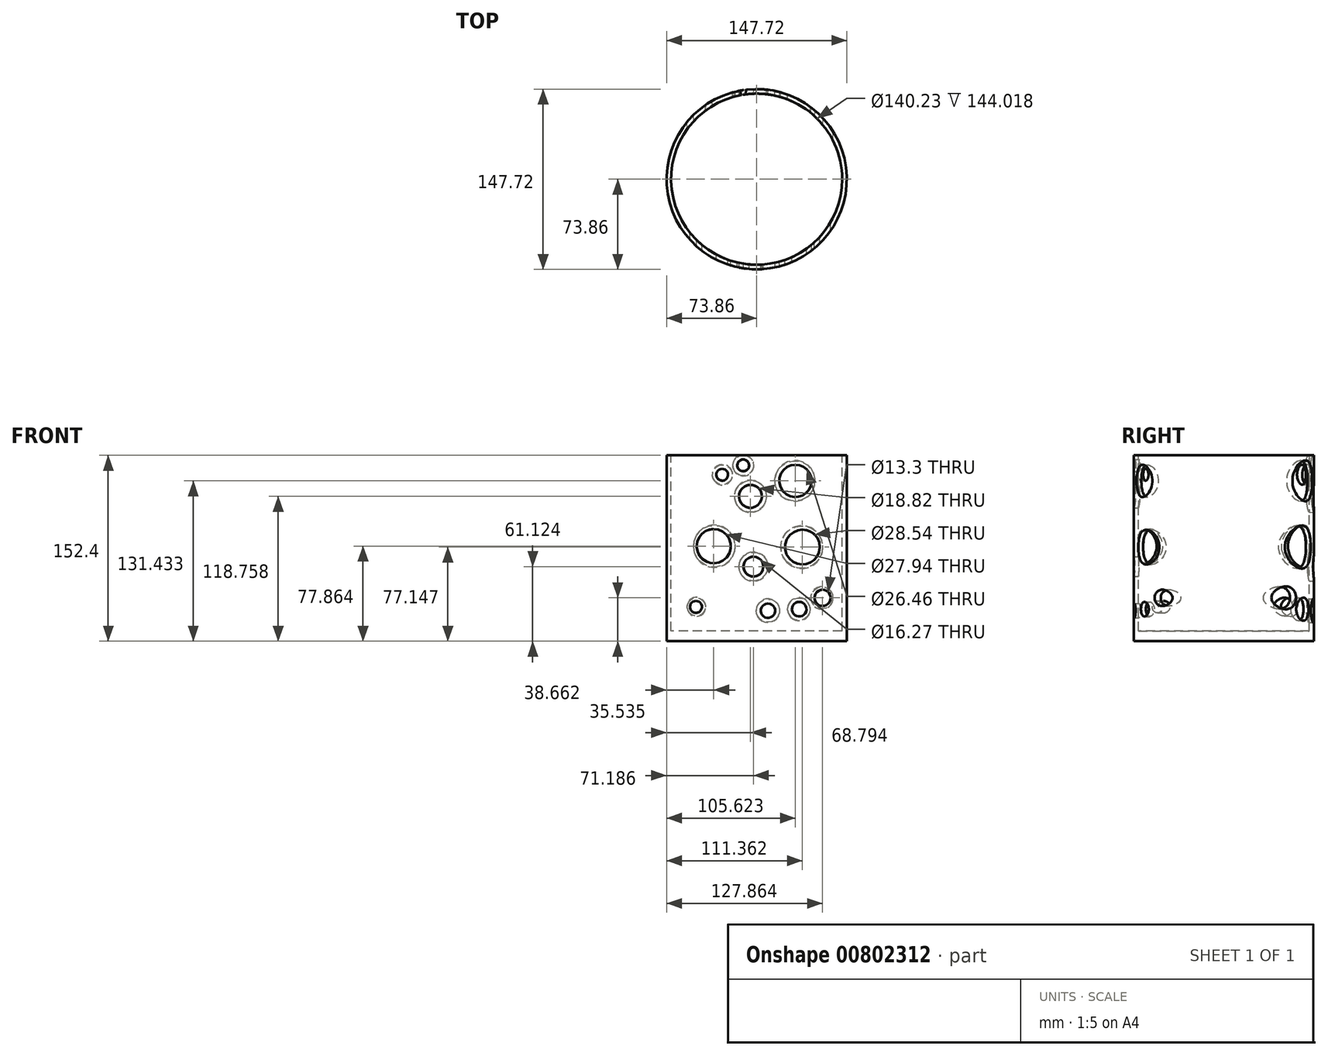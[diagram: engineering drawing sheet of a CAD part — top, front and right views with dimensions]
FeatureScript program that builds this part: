
annotation { "Feature Type Name" : "Feature", "Feature Type Description" : "" }
export const myFeature = defineFeature(function(context is Context, id is Id, definition is map)
    precondition{}
    {
        {
            var Q0;
            Q0=qCreatedBy(makeId("Top.planeOp"),FACE);
            var sketch = newSketch(context, id + "F0", { "sketchPlane" : qUnion([Q0])});
            skCircle(sketch, "E0", {"center": v(0, 0) * mm, "radius": 73.86 * mm});
            skSolve(sketch);
        }
        {
            var Q0;
            Q0=makeQuery(id+"F0.imprint","IMPRINT",FACE,{"disambiguationData":[TD([[makeQuery(id+"F0.imprint","IMPRINT",EDGE,{"derivedFrom":sQuery(id+"F0.wireOp",EDGE,"E0")}),1.0]])]});
            extrude(context, id + "F1", {"entities" : qUnion([Q0]), "depth" : 152.4 * mm, "offsetDistance" : 25.4 * mm});
        }
        {
            var Q0;
            Q0=makeQuery(id+"F1.opExtrude","CAP_FACE",FACE,{"disambiguationData":[OSD([sQuery(id+"F0.wireOp",EDGE,"E0")])],"isStart":false});
            var sketch = newSketch(context, id + "F2", { "sketchPlane" : qUnion([Q0])});
            skCircle(sketch, "E1", {"center": v(0, 0) * mm, "radius": 70.12 * mm});
            skSolve(sketch);
        }
        {
            var Q0;
            Q0 = qSketchRegion(id + "F2", true);
            extrude(context, id + "F3", {"entities" : qUnion([Q0]), "operationType" : NewBodyOperationType.REMOVE, "oppositeDirection" : true, "depth" : 144.02 * mm, "offsetDistance" : 25.4 * mm});
        }
        {
            var Q0;
            Q0=qCreatedBy(makeId("Front.planeOp"),FACE);
            var sketch = newSketch(context, id + "F4", { "sketchPlane" : qUnion([Q0])});
            skCircle(sketch, "E2", {"center": v(-11.04, 144.1) * mm, "radius": 4.84 * mm});
            skCircle(sketch, "E3", {"center": v(-28.26, 136.46) * mm, "radius": 4.84 * mm});
            skCircle(sketch, "E4", {"center": v(-5.07, 118.76) * mm, "radius": 9.41 * mm});
            skCircle(sketch, "E5", {"center": v(37.5, 77.15) * mm, "radius": 14.27 * mm});
            skCircle(sketch, "E6", {"center": v(-35.2, 77.86) * mm, "radius": 13.97 * mm});
            skCircle(sketch, "E7", {"center": v(31.76, 131.43) * mm, "radius": 13.23 * mm});
            skCircle(sketch, "E8", {"center": v(-2.67, 61.12) * mm, "radius": 8.13 * mm});
            skCircle(sketch, "E9", {"center": v(-49.79, 28.12) * mm, "radius": 4.9 * mm});
            skCircle(sketch, "E10", {"center": v(9.28, 25.01) * mm, "radius": 5.9 * mm});
            skCircle(sketch, "E11", {"center": v(54, 35.54) * mm, "radius": 6.65 * mm});
            skCircle(sketch, "E12", {"center": v(34.87, 26.2) * mm, "radius": 6 * mm});
            skSolve(sketch);
        }
        {
            var Q0;
            Q0 = qSketchRegion(id + "F4", true);
            extrude(context, id + "F5", {"entities" : qUnion([Q0]), "operationType" : NewBodyOperationType.REMOVE, "oppositeDirection" : true, "depth" : 117.35 * mm, "offsetDistance" : 25.4 * mm, "hasDraft" : true, "draftAngle" : 3 * degree});
        }
        {
            var Q0;
            Q0 = qSketchRegion(id + "F4", true);
            extrude(context, id + "F6", {"entities" : qUnion([Q0]), "operationType" : NewBodyOperationType.REMOVE, "depth" : 211.84 * mm, "offsetDistance" : 25.4 * mm});
        }
    });
